# Revit family: LR3332-W-2-RM
name_source: partatom
category: Plumbing Fixtures
revit_build: Autodesk Revit MEP 2016 (Build: 20150220_1215(x64)
units: mm (PartAtom-declared; Revit-internal decimal feet)

## family parameters
Cut with Voids When Loaded = No
Host = Face
OmniClass Number = 23.45.05.21.11.11
OmniClass Title = Water Operated Water Closets
Part Type = Normal
Room Calculation Point = No
Round Connector Dimension = Use Diameter
Shared = Yes

## types (2) — shared parameters
CW Connection = Yes
LR3332-W-2 - Ligature Resistant Siphon Jet Toilet - On Floor Replacement = Yes
Material = Stainless Steel
Tempered Water Connection = No
Vent Connection = No
W- Wall (Concealed) = Yes
Waste Connection = Yes
zero-valued in all types: Amperage, CWFU, HWFU, Voltage, WFU

## per-type parameters (varying)
- LR3332-W-2: - 1.28 GPF (HET)=No; - 1.6 GPF (Not Available in California)=No; 2- On Floor, Wall Outlet Toilet=Yes; 3395 - Anchoring Assembly=No; ADA- 18" ADA Integral Seat Height=No; CI - Cycle Interrupt for Time-Trol Valves=No; CO1- Cleanout with O-Ring to NO-Hub 2-3/8" x 4" (Plain End)=No; CO1_3 - Cleanout with O-Ring to NO-Hub 2-3/8" x 3" (Plain End)=No; COH - Cleanout Hook Assembly (-PE & Rear Mount Only)=No; Default Elevation=15"; Description=Ligature Resistant BlowOut Jet Toilet; EG- Enviro-Glaze Color Specify   Toilet Exterior &  Toilet Interior=No; EGE -  Enviro-Glaze Color  Specify  Toilet Exterior Only=No; EVSFV - Master-Trol Electronic Flush Valve (N/A for Top Supply)=No; FT - Flood-Trol (N/A w/ Top Supply)=No; FTA - Flood-Trol Auto-Reset (N/A w/ Top Supply)=No; FTE - Flood-Trol Electronic=No; FV- Flush Valve, Mechanical (N/A for ADA)=No; FVBO- Flush Valv by Others=No; FVH- Flush Valve, Hydraulic (N/A for Top Supply)=No; FVT- Flush Valve Thru-Wall Connection=No; HPS - High Polish Integral Seat=No; HW Connection=No; MTPFV - Master-Trol® PLUS Electronic Flush Valve (N/A for Top Supply)=No; MVCFV- Time-trol Electronic F.V. (N/A for Top Supply)=No; Manufacturer=Acorn Engineering Co.; Model=2140-W-2-RM; PC-Pinned Cleanout Plug (-PE & Rear Mount Only)=No; PE - Plain End Waste (Only w/ Rear Mount)=No; Revised Date=09/20/18; T- Top (Exposed ) (LRFVC Required)=No; TF- Transformer, 120VAC to 24VAC (-MVCFV option)=No; TSC - Toilet Shipping Cover=No; TWE - Toilet Waste Extension (-PE & Rear Mount Only) Specify Length Beyond Fixture=No; URL=https://www.acorneng.com
- Must Match Filename: - 1.28 GPF (HET)=Yes; - 1.6 GPF (Not Available in California)=Yes; 2- On Floor, Wall Outlet Toilet=No; 3395 - Anchoring Assembly=Yes; ADA- 18" ADA Integral Seat Height=Yes; CI - Cycle Interrupt for Time-Trol Valves=Yes; CO1- Cleanout with O-Ring to NO-Hub 2-3/8" x 4" (Plain End)=Yes; CO1_3 - Cleanout with O-Ring to NO-Hub 2-3/8" x 3" (Plain End)=Yes; COH - Cleanout Hook Assembly (-PE & Rear Mount Only)=Yes; Default Elevation=34"; Description=Description Must Match Submittal Description; EG- Enviro-Glaze Color Specify   Toilet Exterior &  Toilet Interior=Yes; EGE -  Enviro-Glaze Color  Specify  Toilet Exterior Only=Yes; EVSFV - Master-Trol Electronic Flush Valve (N/A for Top Supply)=Yes; FT - Flood-Trol (N/A w/ Top Supply)=Yes; FTA - Flood-Trol Auto-Reset (N/A w/ Top Supply)=Yes; FTE - Flood-Trol Electronic=Yes; FV- Flush Valve, Mechanical (N/A for ADA)=Yes; FVBO- Flush Valv by Others=Yes; FVH- Flush Valve, Hydraulic (N/A for Top Supply)=Yes; FVT- Flush Valve Thru-Wall Connection=Yes; HPS - High Polish Integral Seat=Yes; HW Connection=Yes; MTPFV - Master-Trol® PLUS Electronic Flush Valve (N/A for Top Supply)=Yes; MVCFV- Time-trol Electronic F.V. (N/A for Top Supply)=Yes; Manufacturer=Use appropriate company name, refer to Acorn-Revit Style Guide; Model=Model#-Options, example:  1415-CT-1; PC-Pinned Cleanout Plug (-PE & Rear Mount Only)=Yes; PE - Plain End Waste (Only w/ Rear Mount)=Yes; Revised Date=example:  05/28/11; T- Top (Exposed ) (LRFVC Required)=Yes; TF- Transformer, 120VAC to 24VAC (-MVCFV option)=Yes; TSC - Toilet Shipping Cover=Yes; TWE - Toilet Waste Extension (-PE & Rear Mount Only) Specify Length Beyond Fixture=Yes; URL=Use appropriate URL, refer to Acorn-Revit Style Guide

## geometry (parser evidence)
native form markers: Sweep x1
no freeform markers — native parametric forms only
